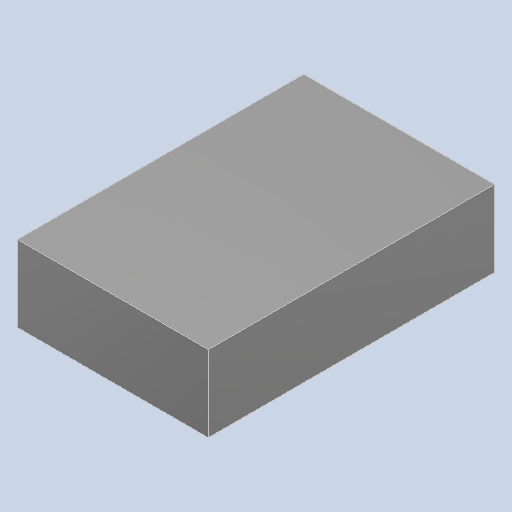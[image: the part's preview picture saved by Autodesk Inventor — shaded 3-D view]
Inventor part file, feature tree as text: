
AUTODESK INVENTOR PART (.ipt)
format: ipt  version: 2022 (Build 260153000, 153)  size: 85,504 bytes
history: imported  units: in
note: dims shown in document units (in); Inventor stores cm internally (conversion verified against a paired STEP export)
features: imported_body x1
ambient origin geometry x8: Origin, YZ Plane, XZ Plane, XY Plane, X Axis, Y Axis, Z Axis, Center Point
bodies: Solid1 (imported_parasolid)
feature tree (1):
  imported_body  NMx_Import_Brep_tag  [imported B-rep: ~6 faces, bbox_mm=[2.0, 0.8, 3.0]]
